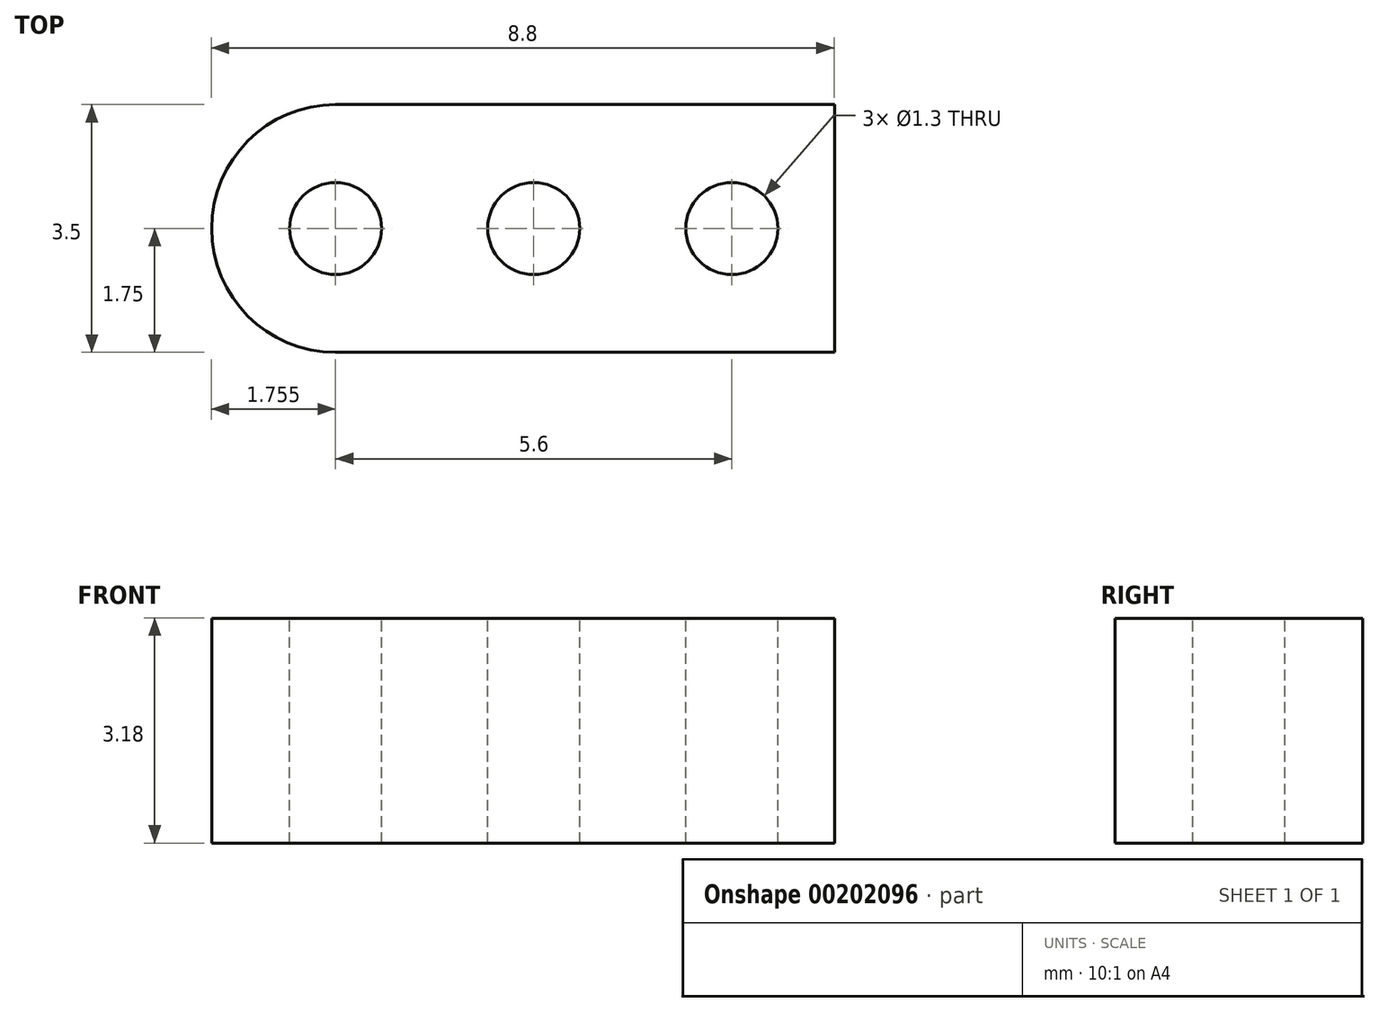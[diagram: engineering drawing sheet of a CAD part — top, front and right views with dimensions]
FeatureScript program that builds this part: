
annotation { "Feature Type Name" : "Feature", "Feature Type Description" : "" }
export const myFeature = defineFeature(function(context is Context, id is Id, definition is map)
    precondition{}
    {
        {
            var Q0;
            Q0=qCreatedBy(makeId("Top.planeOp"),FACE);
            var sketch = newSketch(context, id + "F0", { "sketchPlane" : qUnion([Q0])});
            skLineSegment(sketch, "E0.bottom", {"start": v(-3.53, 1.75) * mm, "end": v(3.53, 1.75) * mm});
            skLineSegment(sketch, "E0.top", {"start": v(-3.53, -1.75) * mm, "end": v(3.52, -1.75) * mm});
            skLineSegment(sketch, "E0.left", {"start": v(-3.53, 1.75) * mm, "end": v(-3.53, -1.75) * mm});
            skLineSegment(sketch, "E0.right", {"start": v(3.53, 1.75) * mm, "end": v(3.52, -1.75) * mm});
            skPoint(sketch, "E0.middle", {"position": v(0, 0) * mm});
            skArc(sketch, "E1", {"start": v(-3.53, 1.75) * mm, "mid": v(-5.28, 0) * mm, "end": v(-3.53, -1.75) * mm});
            skSolve(sketch);
        }
        {
            var Q0;
            Q0=qSketchRegion(id+"F0",true);
            extrude(context, id + "F1", {"entities" : qUnion([Q0]), "depth" : 3.17 * mm});
        }
        {
            var Q0;
            Q0=makeQuery(id+"F1.opExtrude","CAP_FACE",FACE,{"disambiguationData":[OSD([sQuery(id+"F0.wireOp",EDGE,"E0.bottom"),sQuery(id+"F0.wireOp",EDGE,"E0.top"),sQuery(id+"F0.wireOp",EDGE,"E0.right"),sQuery(id+"F0.wireOp",EDGE,"E1")])],"isStart":false});
            var sketch = newSketch(context, id + "F2", { "sketchPlane" : qUnion([Q0])});
            skPoint(sketch, "E2", {"position": v(0, 0) * mm});
            skPoint(sketch, "E3", {"position": v(-0.73, 0) * mm});
            skPoint(sketch, "E4", {"position": v(-3.53, 0) * mm});
            skPoint(sketch, "E5", {"position": v(2.07, 0) * mm});
            skSolve(sketch);
        }
        {
            var Q0;
            Q0=sQuery(id+"F2.wireOp",VERTEX,"E3");
            var Q1;
            Q1=sQuery(id+"F2.wireOp",VERTEX,"E4");
            var Q2;
            Q2=sQuery(id+"F2.wireOp",VERTEX,"E5");
            var Q3;
            Q3=makeQuery(id+"F1.opExtrude","SWEPT_BODY",BODY,{"disambiguationData":[OSD([sQuery(id+"F0.wireOp",EDGE,"E0.bottom"),sQuery(id+"F0.wireOp",EDGE,"E0.top"),sQuery(id+"F0.wireOp",EDGE,"E0.right"),sQuery(id+"F0.wireOp",EDGE,"E1")])]});
            hole(context, id + "F3", {"style" : HoleStyle.SIMPLE, "endStyle" : HoleEndStyle.THROUGH, "holeDiameter" : 1.3 * mm, "locations" : qUnion([Q0, Q1, Q2]), "scope" : qUnion([Q3]), "isTappedThrough" : true});
        }
    });
